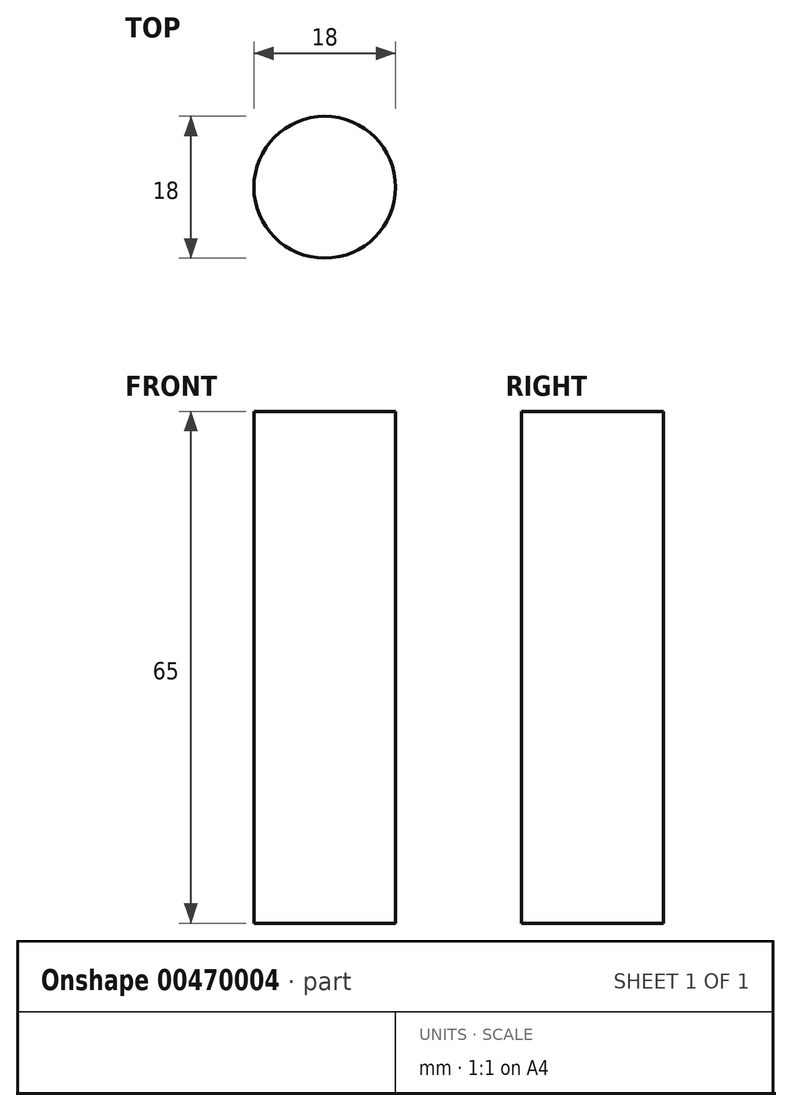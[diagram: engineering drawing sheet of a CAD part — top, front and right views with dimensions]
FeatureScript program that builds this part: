
annotation { "Feature Type Name" : "Feature", "Feature Type Description" : "" }
export const myFeature = defineFeature(function(context is Context, id is Id, definition is map)
    precondition{}
    {
        {
            var Q0;
            Q0=qCreatedBy(makeId("Top.planeOp"),FACE);
            var sketch = newSketch(context, id + "F0", { "sketchPlane" : qUnion([Q0])});
            skCircle(sketch, "E0", {"center": v(0, 0) * mm, "radius": 9 * mm});
            skSolve(sketch);
        }
        {
            var Q0;
            Q0 = qSketchRegion(id + "F0", true);
            extrude(context, id + "F1", {"entities" : qUnion([Q0]), "endBound" : BoundingType.SYMMETRIC, "depth" : 65 * mm, "offsetDistance" : 25 * mm});
        }
    });
